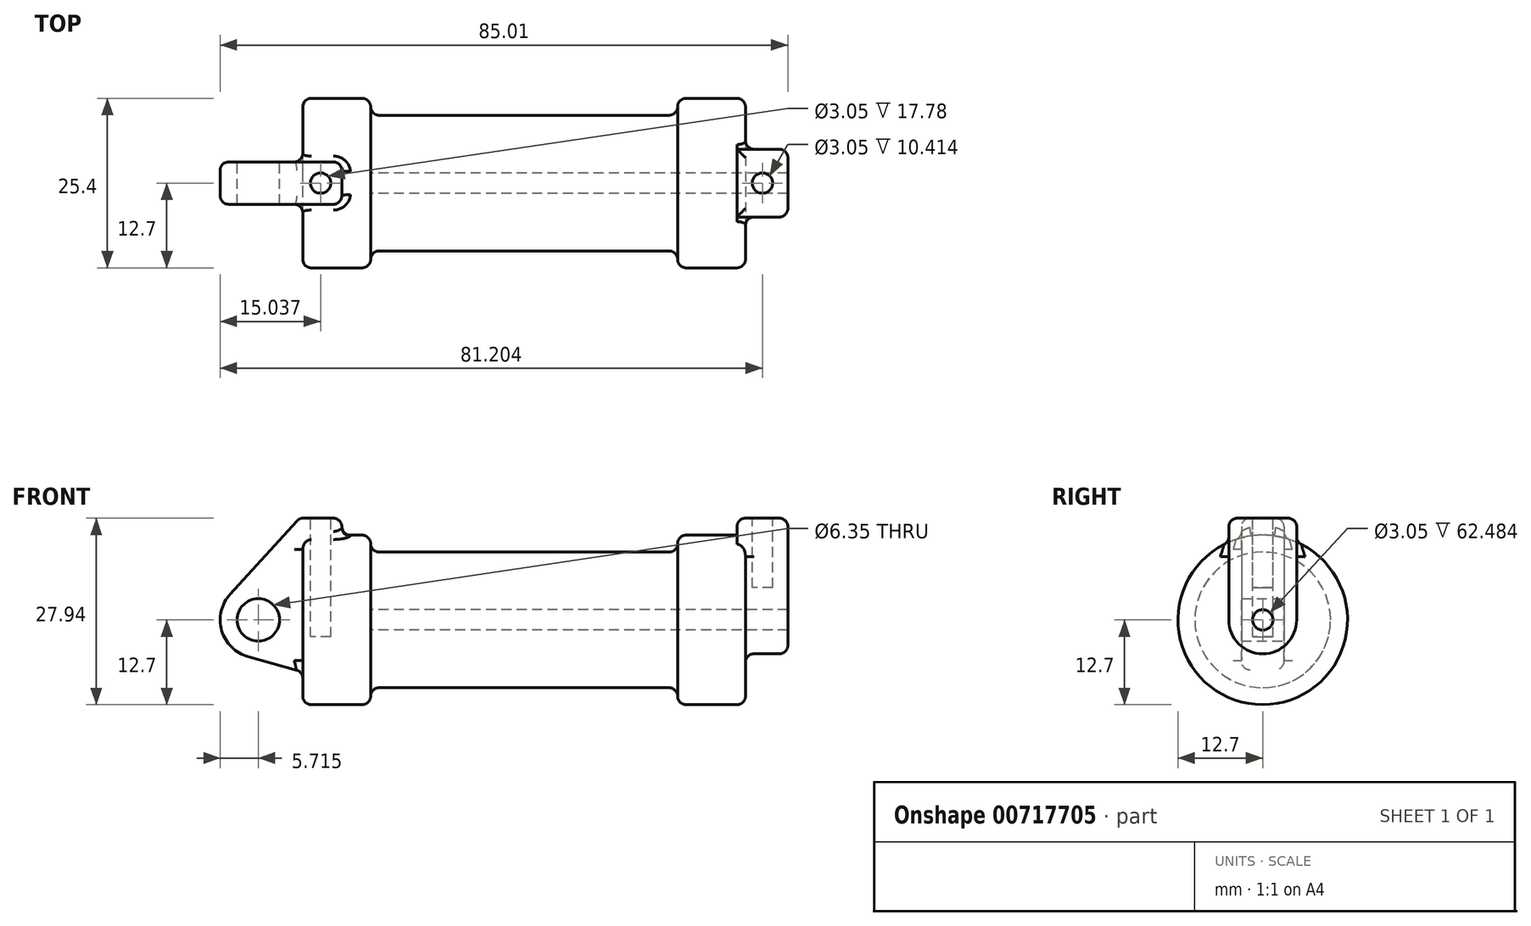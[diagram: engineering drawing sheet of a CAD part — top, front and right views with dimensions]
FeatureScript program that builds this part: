
annotation { "Feature Type Name" : "Feature", "Feature Type Description" : "" }
export const myFeature = defineFeature(function(context is Context, id is Id, definition is map)
    precondition{}
    {
        {
            var Q0;
            Q0=qCreatedBy(makeId("Front.planeOp"),FACE);
            var sketch = newSketch(context, id + "F0", { "sketchPlane" : qUnion([Q0])});
            skLineSegment(sketch, "E0", {"start": v(0, 0) * mm, "end": v(0, 12.7) * mm});
            skLineSegment(sketch, "E1", {"start": v(0, 12.7) * mm, "end": v(10.16, 12.7) * mm});
            skLineSegment(sketch, "E2", {"start": v(10.16, 12.7) * mm, "end": v(10.16, 10.16) * mm});
            skLineSegment(sketch, "E3", {"start": v(10.16, 10.16) * mm, "end": v(56.13, 10.16) * mm});
            skLineSegment(sketch, "E4", {"start": v(56.13, 10.16) * mm, "end": v(56.13, 12.7) * mm});
            skLineSegment(sketch, "E5", {"start": v(56.13, 12.7) * mm, "end": v(66.3, 12.7) * mm});
            skLineSegment(sketch, "E6", {"start": v(66.3, 12.7) * mm, "end": v(66.3, 0) * mm});
            skLineSegment(sketch, "E7", {"start": v(66.3, 0) * mm, "end": v(0, 0) * mm});
            skLineSegment(sketch, "E8", {"start": v(5.84, 15.24) * mm, "end": v(-0.5, 15.24) * mm});
            skLineSegment(sketch, "E9", {"start": v(-0.5, 15.24) * mm, "end": v(-10.88, 3.85) * mm});
            skLineSegment(sketch, "E10", {"start": v(0, 0) * mm, "end": v(-6.65, 0) * mm});
            skCircle(sketch, "E11", {"center": v(-6.65, 0) * mm, "radius": 5.72 * mm});
            skCircle(sketch, "E12", {"center": v(-6.65, 0) * mm, "radius": 3.18 * mm});
            skLineSegment(sketch, "E13", {"start": v(5.84, 15.24) * mm, "end": v(5.84, -9.4) * mm});
            skLineSegment(sketch, "E14", {"start": v(5.84, -9.4) * mm, "end": v(-8.18, -5.5) * mm});
            skSolve(sketch);
        }
        {
            var Q0;
            {var subQ0=sQuery(id+"F0.wireOp",EDGE,"E2");Q0=makeQuery(id+"F0.imprint","IMPRINT",FACE,{"disambiguationData":[TD([[makeQuery(id+"F0.imprint","IMPRINT",EDGE,{"derivedFrom":subQ0}),-1.0]])]});}
            var Q1;
            {var subQ0=sQuery(id+"F0.wireOp",EDGE,"E0");Q1=makeQuery(id+"F0.imprint","IMPRINT",FACE,{"disambiguationData":[TD([[makeQuery(id+"F0.imprint","IMPRINT",EDGE,{"derivedFrom":subQ0}),-1.0]])]});}
            var Q2;
            Q2=sQuery(id+"F0.wireOp",EDGE,"E7");
            revolve(context, id + "F1", {"entities" : qUnion([Q0, Q1]), "axis" : qUnion([Q2]), "revolveType" : RevolveType.FULL, "surfaceOperationType" : NewSurfaceOperationType.NEW});
        }
        {
            var Q0;
            {var subQ3=sQuery(id+"F0.wireOp",EDGE,"E0");Q0=makeQuery(id+"F0.imprint","IMPRINT",FACE,{"disambiguationData":[TD([[makeQuery(id+"F0.imprint","IMPRINT",EDGE,{"derivedFrom":subQ3}),1.0]])]});}
            var Q1;
            {var subQ4=sQuery(id+"F0.wireOp",EDGE,"E12");Q1=makeQuery(id+"F0.imprint","IMPRINT",FACE,{"disambiguationData":[TD([[makeQuery(id+"F0.imprint","IMPRINT",EDGE,{"derivedFrom":subQ4}),-1.0]])]});}
            var Q2;
            {var subQ0=sQuery(id+"F0.wireOp",EDGE,"E14");Q2=makeQuery(id+"F0.imprint","IMPRINT",FACE,{"disambiguationData":[TD([[makeQuery(id+"F0.imprint","IMPRINT",EDGE,{"derivedFrom":subQ0}),-1.0]])]});}
            var Q3;
            {var subQ0=sQuery(id+"F0.wireOp",EDGE,"E0");Q3=makeQuery(id+"F0.imprint","IMPRINT",FACE,{"disambiguationData":[TD([[makeQuery(id+"F0.imprint","IMPRINT",EDGE,{"derivedFrom":subQ0}),-1.0]])]});}
            extrude(context, id + "F2", {"entities" : qUnion([Q0, Q1, Q2, Q3]), "operationType" : NewBodyOperationType.ADD, "endBound" : BoundingType.SYMMETRIC, "depth" : 6.35 * mm, "offsetDistance" : 25.4 * mm});
        }
        {
            var Q0;
            Q0=makeQuery(id+"F1.opRevolve","SWEPT_FACE",FACE,{"disambiguationData":[OSD([sQuery(id+"F0.wireOp",EDGE,"E6")])]});
            var sketch = newSketch(context, id + "F3", { "sketchPlane" : qUnion([Q0])});
            skCircle(sketch, "E15", {"center": v(0, 0) * mm, "radius": 1.52 * mm});
            skCircle(sketch, "E16", {"center": v(0, 0) * mm, "radius": 5.08 * mm});
            skLineSegment(sketch, "E17", {"start": v(-5.08, 0) * mm, "end": v(-5.08, 15.24) * mm});
            skLineSegment(sketch, "E18", {"start": v(-5.08, 15.24) * mm, "end": v(5.08, 15.24) * mm});
            skLineSegment(sketch, "E19", {"start": v(5.08, 15.24) * mm, "end": v(5.08, 0) * mm});
            skSolve(sketch);
        }
        {
            var Q0;
            {var subQ0=sQuery(id+"F3.wireOp",EDGE,"E18");Q0=makeQuery(id+"F3.imprint","IMPRINT",FACE,{"disambiguationData":[TD([[makeQuery(id+"F3.imprint","IMPRINT",EDGE,{"derivedFrom":subQ0}),-1.0]])]});}
            extrude(context, id + "F4", {"entities" : qUnion([Q0]), "operationType" : NewBodyOperationType.ADD, "oppositeDirection" : true, "depth" : 1.27 * mm, "offsetDistance" : 25.4 * mm});
        }
        {
            var Q0;
            {var subQ0=sQuery(id+"F3.wireOp",EDGE,"E18");Q0=makeQuery(id+"F3.imprint","IMPRINT",FACE,{"disambiguationData":[TD([[makeQuery(id+"F3.imprint","IMPRINT",EDGE,{"derivedFrom":subQ0}),-1.0]])]});}
            var Q1;
            {var subQ0=sQuery(id+"F3.wireOp",EDGE,"E17");var subQ1=sQuery(id+"F3.wireOp",EDGE,"E16");var subQ2=makeQuery(id+"F3.imprint","INTERSECT",VERTEX,{"derivedFrom":[subQ1,subQ0]});Q1=makeQuery(id+"F3.imprint","IMPRINT",FACE,{"disambiguationData":[TD([[makeQuery(id+"F3.imprint","IMPRINT",EDGE,{"disambiguationData":[TD([[subQ2,1.0]])],"derivedFrom":subQ1}),-1.0]])]});}
            var Q2;
            Q2=makeQuery(id+"F3.imprint","IMPRINT",FACE,{"disambiguationData":[TD([[makeQuery(id+"F3.imprint","IMPRINT",EDGE,{"derivedFrom":sQuery(id+"F3.wireOp",EDGE,"E15")}),-1.0]])]});
            extrude(context, id + "F5", {"entities" : qUnion([Q0, Q1, Q2]), "operationType" : NewBodyOperationType.ADD, "depth" : 6.35 * mm, "offsetDistance" : 25.4 * mm});
        }
        {
            var Q0;
            Q0=makeQuery(id+"F3.imprint","IMPRINT",FACE,{"disambiguationData":[TD([[makeQuery(id+"F3.imprint","IMPRINT",EDGE,{"derivedFrom":sQuery(id+"F3.wireOp",EDGE,"E15")}),1.0]])]});
            var Q1;
            Q1=makeQuery(id+"F1.opRevolve","SWEPT_FACE",FACE,{"disambiguationData":[OSD([sQuery(id+"F0.wireOp",EDGE,"E2")])]});
            extrude(context, id + "F6", {"entities" : qUnion([Q0]), "operationType" : NewBodyOperationType.REMOVE, "endBound" : BoundingType.UP_TO_SURFACE, "oppositeDirection" : true, "endBoundEntityFace" : qUnion([Q1]), "depth" : 25.4 * mm, "offsetDistance" : 25.4 * mm});
        }
        {
            var Q0;
            Q0=makeQuery(id+"F2.opExtrude","SWEPT_FACE",FACE,{"disambiguationData":[OSD([sQuery(id+"F0.wireOp",EDGE,"E8")])]});
            var sketch = newSketch(context, id + "F7", { "sketchPlane" : qUnion([Q0])});
            skCircle(sketch, "E20", {"center": v(2.67, 0) * mm, "radius": 1.52 * mm});
            skPoint(sketch, "E20.centerSnap0", {"position": v(-0.5, 0) * mm});
            skPoint(sketch, "E20.centerSnap1", {"position": v(2.67, 3.18) * mm});
            skSolve(sketch);
        }
        {
            var Q0;
            Q0=qSketchRegion(id+"F7",true);
            extrude(context, id + "F8", {"entities" : qUnion([Q0]), "operationType" : NewBodyOperationType.REMOVE, "oppositeDirection" : true, "depth" : 17.78 * mm, "offsetDistance" : 25.4 * mm});
        }
        {
            var Q0;
            {var subQ0=sQuery(id+"F3.wireOp",EDGE,"E18");Q0=makeQuery(id+"F5.boolean.opBoolean","MERGE",FACE,{"derivedFrom":[makeQuery(id+"F4.opExtrude","SWEPT_FACE",FACE,{"disambiguationData":[OSD([subQ0])]}),makeQuery(id+"F5.opExtrude","SWEPT_FACE",FACE,{"disambiguationData":[OSD([subQ0])]})]});}
            var sketch = newSketch(context, id + "F9", { "sketchPlane" : qUnion([Q0])});
            skCircle(sketch, "E21", {"center": v(68.83, 0) * mm, "radius": 1.52 * mm});
            skPoint(sketch, "E21.centerSnap0", {"position": v(65.02, 0) * mm});
            skPoint(sketch, "E21.centerSnap1", {"position": v(68.83, 5.08) * mm});
            skSolve(sketch);
        }
        {
            var Q0;
            Q0=qSketchRegion(id+"F9",true);
            extrude(context, id + "F10", {"entities" : qUnion([Q0]), "operationType" : NewBodyOperationType.REMOVE, "oppositeDirection" : true, "depth" : 10.4 * mm, "offsetDistance" : 25.4 * mm});
        }
        {
            var Q0;
            Q0=makeQuery(id+"F1.opRevolve","SWEPT_EDGE",EDGE,{"disambiguationData":[OSD([sQuery(id+"F0.wireOp",EDGE,"E2"),sQuery(id+"F0.wireOp",EDGE,"E3")])]});
            var Q1;
            Q1=makeQuery(id+"F1.opRevolve","SWEPT_EDGE",EDGE,{"disambiguationData":[OSD([sQuery(id+"F0.wireOp",EDGE,"E1"),sQuery(id+"F0.wireOp",EDGE,"E2")])]});
            var Q2;
            Q2=makeQuery(id+"F1.opRevolve","SWEPT_EDGE",EDGE,{"disambiguationData":[OSD([sQuery(id+"F0.wireOp",EDGE,"E3"),sQuery(id+"F0.wireOp",EDGE,"E4")])]});
            var Q3;
            Q3=makeQuery(id+"F1.opRevolve","SWEPT_EDGE",EDGE,{"disambiguationData":[OSD([sQuery(id+"F0.wireOp",EDGE,"E4"),sQuery(id+"F0.wireOp",EDGE,"E5")])]});
            var Q4;
            Q4=makeQuery(id+"F1.opRevolve","SWEPT_EDGE",EDGE,{"disambiguationData":[OSD([sQuery(id+"F0.wireOp",EDGE,"E5"),sQuery(id+"F0.wireOp",EDGE,"E6")])]});
            var Q5;
            Q5=makeQuery(id+"F1.opRevolve","SWEPT_EDGE",EDGE,{"disambiguationData":[OSD([sQuery(id+"F0.wireOp",EDGE,"E0"),sQuery(id+"F0.wireOp",EDGE,"E1")])]});
            fillet(context, id + "F11", {"entities" : qUnion([Q0, Q1, Q2, Q3, Q4, Q5]), "radius" : 1.27 * mm, "tangentPropagation" : true, "allowEdgeOverflow" : false});
        }
        {
            var Q0;
            Q0=makeQuery(id+"F1.boolean.opBoolean","INTERSECT",EDGE,{"derivedFrom":[makeQuery(id+"F2.opExtrude","CAP_FACE",FACE,{"disambiguationData":[OSD([sQuery(id+"F0.wireOp",EDGE,"E8"),sQuery(id+"F0.wireOp",EDGE,"E9"),sQuery(id+"F0.wireOp",EDGE,"E11"),sQuery(id+"F0.wireOp",EDGE,"E12"),sQuery(id+"F0.wireOp",EDGE,"E13"),sQuery(id+"F0.wireOp",EDGE,"E14")])],"isStart":false}),makeQuery(id+"F1.opRevolve","SWEPT_FACE",FACE,{"disambiguationData":[OSD([sQuery(id+"F0.wireOp",EDGE,"E1")])]})]});
            var Q1;
            Q1=makeQuery(id+"F1.opRevolve","SWEPT_FACE",FACE,{"disambiguationData":[OSD([sQuery(id+"F0.wireOp",EDGE,"E0")])]});
            var Q2;
            Q2=makeQuery(id+"F2.opExtrude","CAP_EDGE",EDGE,{"disambiguationData":[OSD([sQuery(id+"F0.wireOp",EDGE,"E9")])],"isStart":true});
            var Q3;
            Q3=makeQuery(id+"F2.opExtrude","CAP_EDGE",EDGE,{"disambiguationData":[OSD([sQuery(id+"F0.wireOp",EDGE,"E9")])],"isStart":false});
            var Q4;
            Q4=makeQuery(id+"F5.opExtrude","CAP_EDGE",EDGE,{"disambiguationData":[OSD([sQuery(id+"F3.wireOp",EDGE,"E17")])],"isStart":true});
            var Q5;
            Q5=makeQuery(id+"F5.opExtrude","CAP_EDGE",EDGE,{"disambiguationData":[OSD([sQuery(id+"F3.wireOp",EDGE,"E17")])],"isStart":false});
            var Q6;
            {var subQ0=sQuery(id+"F3.wireOp",EDGE,"E18");var subQ1=sQuery(id+"F3.wireOp",EDGE,"E17");Q6=makeQuery(id+"F5.boolean.opBoolean","MERGE",EDGE,{"derivedFrom":[makeQuery(id+"F4.opExtrude","SWEPT_EDGE",EDGE,{"disambiguationData":[OSD([subQ1,subQ0])]}),makeQuery(id+"F5.opExtrude","SWEPT_EDGE",EDGE,{"disambiguationData":[OSD([subQ1,subQ0])]})]});}
            var Q7;
            {var subQ0=sQuery(id+"F3.wireOp",EDGE,"E19");var subQ1=sQuery(id+"F3.wireOp",EDGE,"E18");Q7=makeQuery(id+"F5.boolean.opBoolean","MERGE",EDGE,{"derivedFrom":[makeQuery(id+"F4.opExtrude","SWEPT_EDGE",EDGE,{"disambiguationData":[OSD([subQ1,subQ0])]}),makeQuery(id+"F5.opExtrude","SWEPT_EDGE",EDGE,{"disambiguationData":[OSD([subQ1,subQ0])]})]});}
            var Q8;
            Q8=makeQuery(id+"F4.opExtrude","CAP_EDGE",EDGE,{"disambiguationData":[OSD([sQuery(id+"F3.wireOp",EDGE,"E18")])],"isStart":false});
            var Q9;
            Q9=makeQuery(id+"F5.opExtrude","CAP_EDGE",EDGE,{"disambiguationData":[OSD([sQuery(id+"F3.wireOp",EDGE,"E18")])],"isStart":false});
            var Q10;
            Q10=makeQuery(id+"F2.opExtrude","CAP_EDGE",EDGE,{"disambiguationData":[OSD([sQuery(id+"F0.wireOp",EDGE,"E8")])],"isStart":false});
            var Q11;
            Q11=makeQuery(id+"F2.opExtrude","SWEPT_EDGE",EDGE,{"disambiguationData":[OSD([sQuery(id+"F0.wireOp",EDGE,"E8"),sQuery(id+"F0.wireOp",EDGE,"E9")])]});
            var Q12;
            Q12=makeQuery(id+"F2.opExtrude","CAP_EDGE",EDGE,{"disambiguationData":[OSD([sQuery(id+"F0.wireOp",EDGE,"E8")])],"isStart":true});
            var Q13;
            Q13=makeQuery(id+"F2.opExtrude","SWEPT_EDGE",EDGE,{"disambiguationData":[OSD([sQuery(id+"F0.wireOp",EDGE,"E8"),sQuery(id+"F0.wireOp",EDGE,"E13")])]});
            var Q14;
            Q14=makeQuery(id+"F2.opExtrude","SWEPT_FACE",FACE,{"disambiguationData":[OSD([sQuery(id+"F0.wireOp",EDGE,"E13")])]});
            var Q15;
            Q15=makeQuery(id+"F4.opExtrude","CAP_EDGE",EDGE,{"disambiguationData":[OSD([sQuery(id+"F0.wireOp",EDGE,"E5"),sQuery(id+"F0.wireOp",EDGE,"E6")])],"isStart":false});
            fillet(context, id + "F12", {"entities" : qUnion([Q0, Q1, Q2, Q3, Q4, Q5, Q6, Q7, Q8, Q9, Q10, Q11, Q12, Q13, Q14, Q15]), "radius" : 1.27 * mm, "tangentPropagation" : true, "allowEdgeOverflow" : false});
        }
    });
